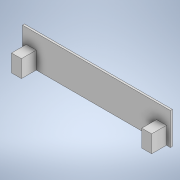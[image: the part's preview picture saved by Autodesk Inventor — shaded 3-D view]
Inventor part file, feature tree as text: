
AUTODESK INVENTOR PART (.ipt)
format: ipt  version: 2020.2 (Build 242310000, 310)  size: 154,112 bytes
history: native  units: mm
features: extrude x3, sketch x3
ambient origin geometry x8: Origin, YZ Plane, XZ Plane, XY Plane, X Axis, Y Axis, Z Axis, Center Point
bodies: Solide1 (feature_tree)
feature tree (6):
  extrude  "Extrusion1"  Depth=300.0mm
  extrude  "Extrusion2"  Depth=65.0mm
  extrude  "Extrusion3"  Depth=4.0mm TaperAngle=0.0deg
  sketch  "Esquisse1"
  sketch  "Esquisse2"
  sketch  "Esquisse3"
